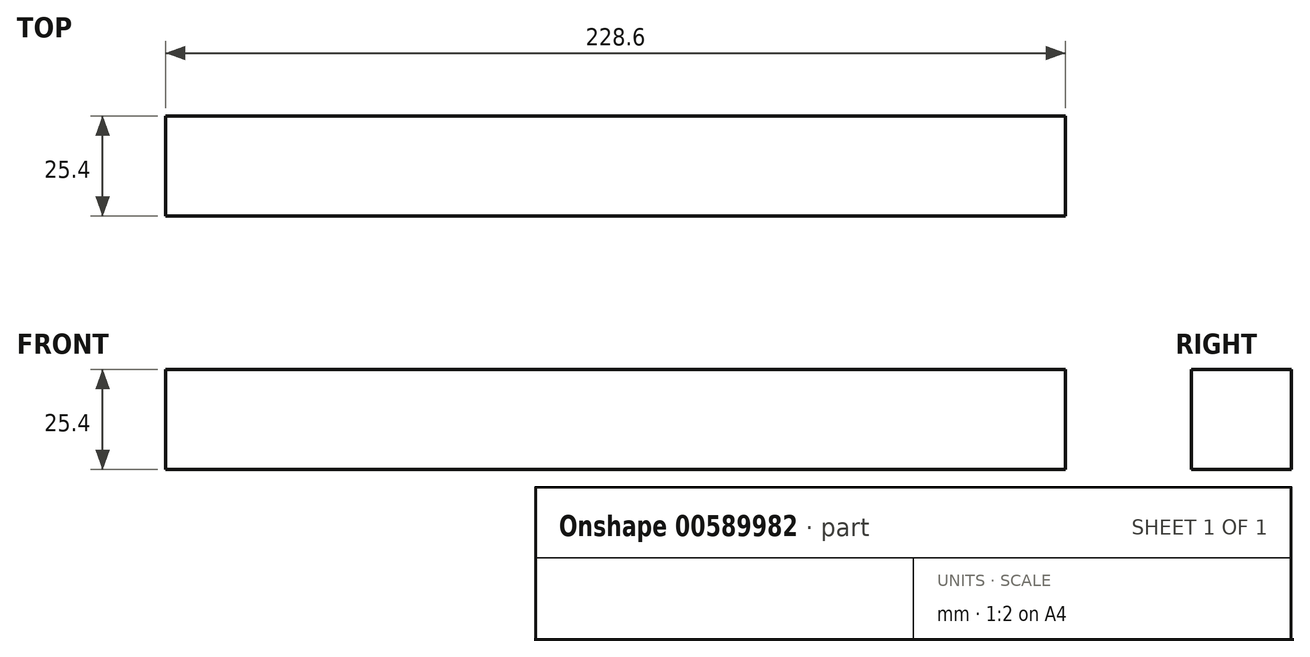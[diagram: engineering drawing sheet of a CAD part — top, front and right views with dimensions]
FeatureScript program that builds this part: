
annotation { "Feature Type Name" : "Feature", "Feature Type Description" : "" }
export const myFeature = defineFeature(function(context is Context, id is Id, definition is map)
    precondition{}
    {
        {
            var Q0;
            Q0=qCreatedBy(makeId("Right.planeOp"),FACE);
            var sketch = newSketch(context, id + "F0", { "sketchPlane" : qUnion([Q0])});
            skLineSegment(sketch, "E0.bottom", {"start": v(0, 0) * mm, "end": v(25.4, 0) * mm});
            skLineSegment(sketch, "E0.top", {"start": v(0, 25.4) * mm, "end": v(25.4, 25.4) * mm});
            skLineSegment(sketch, "E0.left", {"start": v(0, 0) * mm, "end": v(0, 25.4) * mm});
            skLineSegment(sketch, "E0.right", {"start": v(25.4, 0) * mm, "end": v(25.4, 25.4) * mm});
            skSolve(sketch);
        }
        {
            var Q0;
            Q0 = qSketchRegion(id + "F0", true);
            extrude(context, id + "F1", {"entities" : qUnion([Q0]), "depth" : 228.6 * mm, "offsetDistance" : 25.4 * mm});
        }
    });
